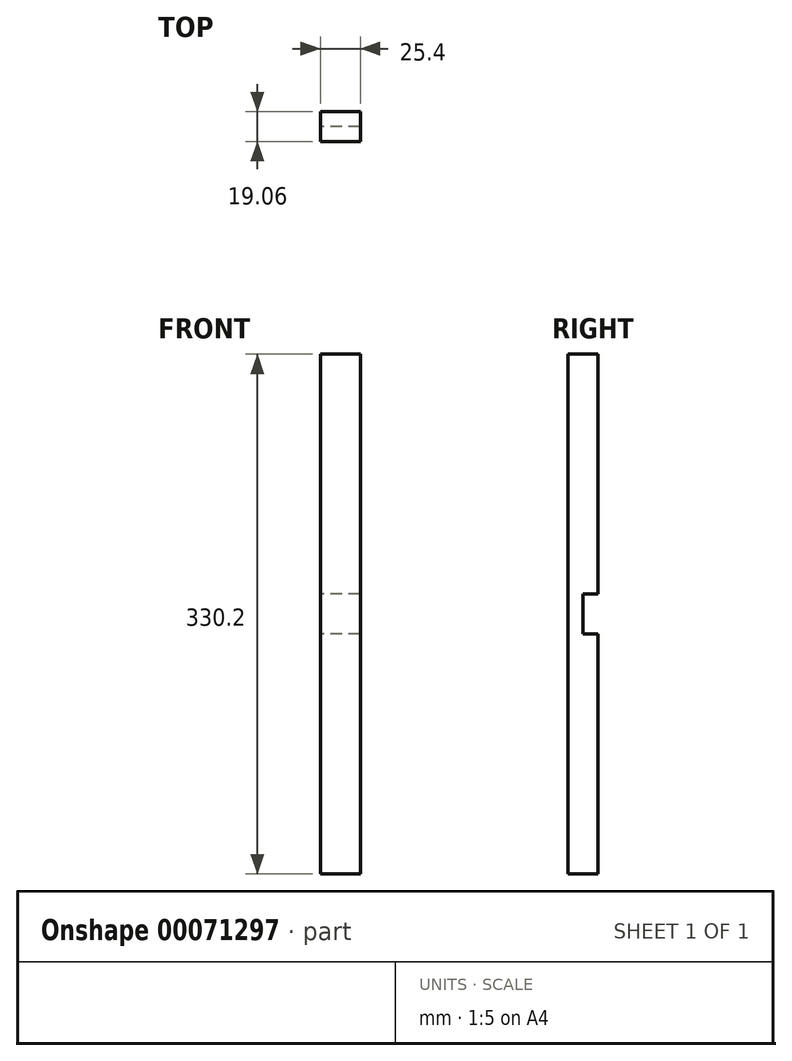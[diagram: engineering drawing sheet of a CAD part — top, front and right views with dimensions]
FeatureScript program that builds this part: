
annotation { "Feature Type Name" : "Feature", "Feature Type Description" : "" }
export const myFeature = defineFeature(function(context is Context, id is Id, definition is map)
    precondition{}
    {
        {
            var Q0;
            Q0=qCreatedBy(makeId("Front.planeOp"),FACE);
            var sketch = newSketch(context, id + "F0", { "sketchPlane" : qUnion([Q0])});
            skLineSegment(sketch, "E0.bottom", {"start": v(-12.7, 165.1) * mm, "end": v(12.7, 165.1) * mm});
            skLineSegment(sketch, "E0.top", {"start": v(-12.7, -165.1) * mm, "end": v(12.7, -165.1) * mm});
            skLineSegment(sketch, "E0.left", {"start": v(-12.7, 165.1) * mm, "end": v(-12.7, -165.1) * mm});
            skLineSegment(sketch, "E0.right", {"start": v(12.7, 165.1) * mm, "end": v(12.7, -165.1) * mm});
            skSolve(sketch);
        }
        {
            var Q0;
            Q0=makeQuery(id+"F0.imprint","IMPRINT",FACE,{"disambiguationData":[TD([[makeQuery(id+"F0.imprint","IMPRINT",EDGE,{"derivedFrom":sQuery(id+"F0.wireOp",EDGE,"E0.bottom")}),-1.0]])]});
            extrude(context, id + "F1", {"entities" : qUnion([Q0]), "endBound" : BoundingType.SYMMETRIC, "depth" : 19.05 * mm});
        }
        {
            var Q0;
            Q0=makeQuery(id+"F1.opExtrude","CAP_FACE",FACE,{"disambiguationData":[OSD([sQuery(id+"F0.wireOp",EDGE,"E0.bottom"),sQuery(id+"F0.wireOp",EDGE,"E0.top"),sQuery(id+"F0.wireOp",EDGE,"E0.left"),sQuery(id+"F0.wireOp",EDGE,"E0.right")])],"isStart":true});
            var sketch = newSketch(context, id + "F2", { "sketchPlane" : qUnion([Q0])});
            skLineSegment(sketch, "E1.bottom", {"start": v(-12.7, 12.7) * mm, "end": v(12.7, 12.7) * mm});
            skLineSegment(sketch, "E1.top", {"start": v(-12.7, -12.7) * mm, "end": v(12.7, -12.7) * mm});
            skLineSegment(sketch, "E1.left", {"start": v(-12.7, 12.7) * mm, "end": v(-12.7, -12.7) * mm});
            skLineSegment(sketch, "E1.right", {"start": v(12.7, 12.7) * mm, "end": v(12.7, -12.7) * mm});
            skSolve(sketch);
        }
        {
            var Q0;
            Q0=makeQuery(id+"F2.imprint","IMPRINT",FACE,{"disambiguationData":[TD([[makeQuery(id+"F2.imprint","IMPRINT",EDGE,{"derivedFrom":sQuery(id+"F2.wireOp",EDGE,"E1.bottom")}),-1.0]])]});
            extrude(context, id + "F3", {"entities" : qUnion([Q0]), "operationType" : NewBodyOperationType.REMOVE, "oppositeDirection" : true, "depth" : 9.52 * mm});
        }
    });
